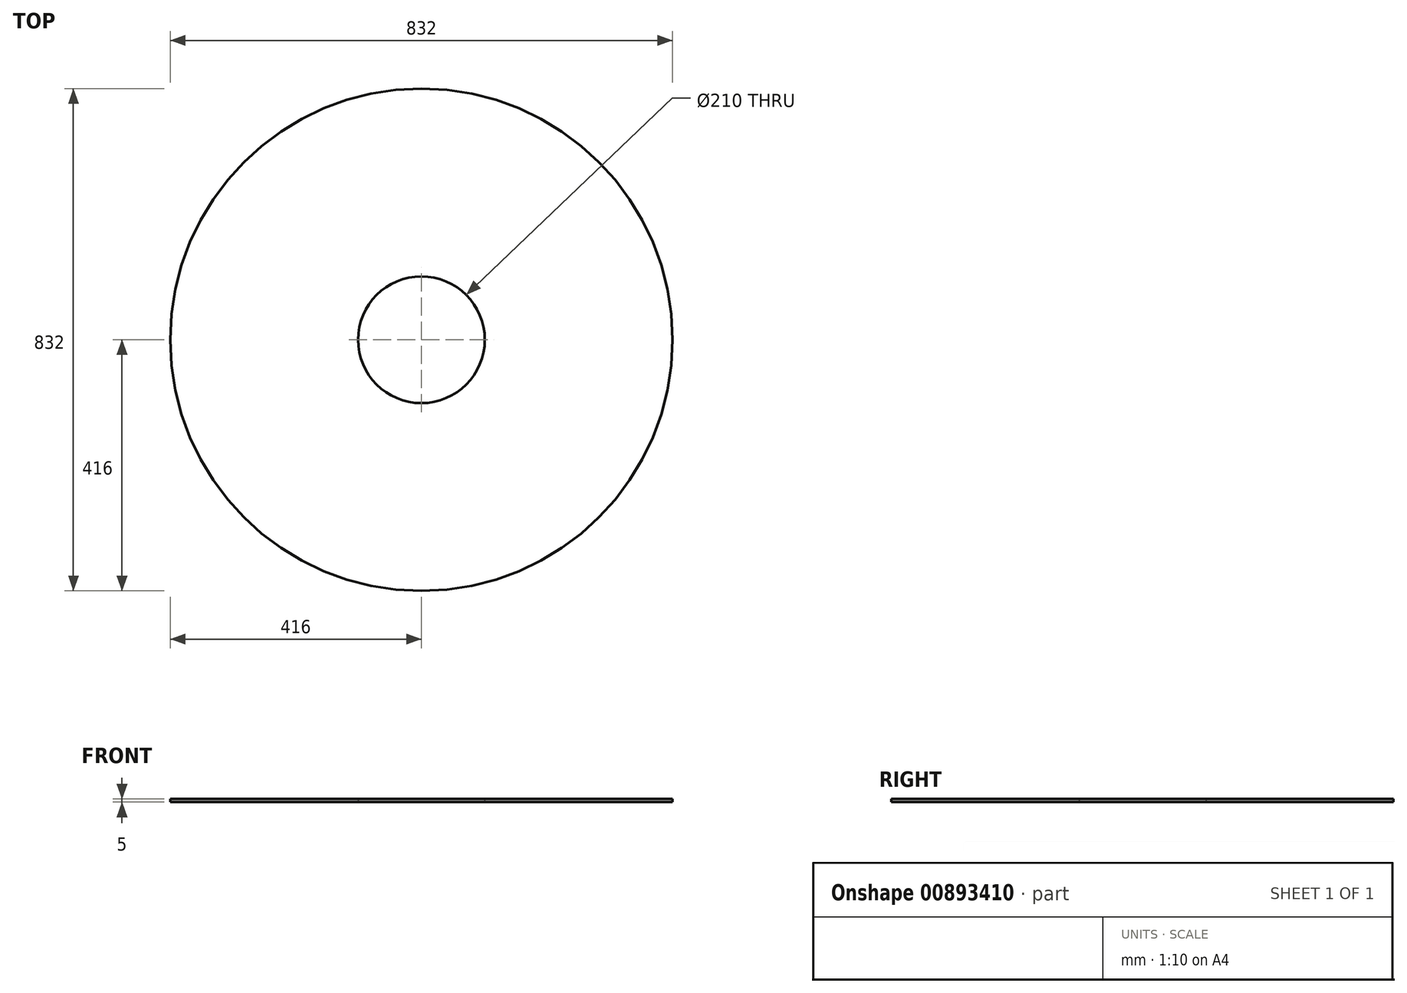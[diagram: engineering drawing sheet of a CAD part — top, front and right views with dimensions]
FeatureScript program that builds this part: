
annotation { "Feature Type Name" : "Feature", "Feature Type Description" : "" }
export const myFeature = defineFeature(function(context is Context, id is Id, definition is map)
    precondition{}
    {
        {
            var Q0;
            Q0=qCreatedBy(makeId("Top.planeOp"),FACE);
            var sketch = newSketch(context, id + "F0", { "sketchPlane" : qUnion([Q0])});
            skCircle(sketch, "E0", {"center": v(0, 0) * mm, "radius": 416 * mm});
            skCircle(sketch, "E1", {"center": v(0, 0) * mm, "radius": 105 * mm});
            skSolve(sketch);
        }
        {
            var Q0;
            Q0 = qSketchRegion(id + "F0", true);
            extrude(context, id + "F1", {"entities" : qUnion([Q0]), "depth" : 5 * mm, "offsetDistance" : 25 * mm});
        }
    });
